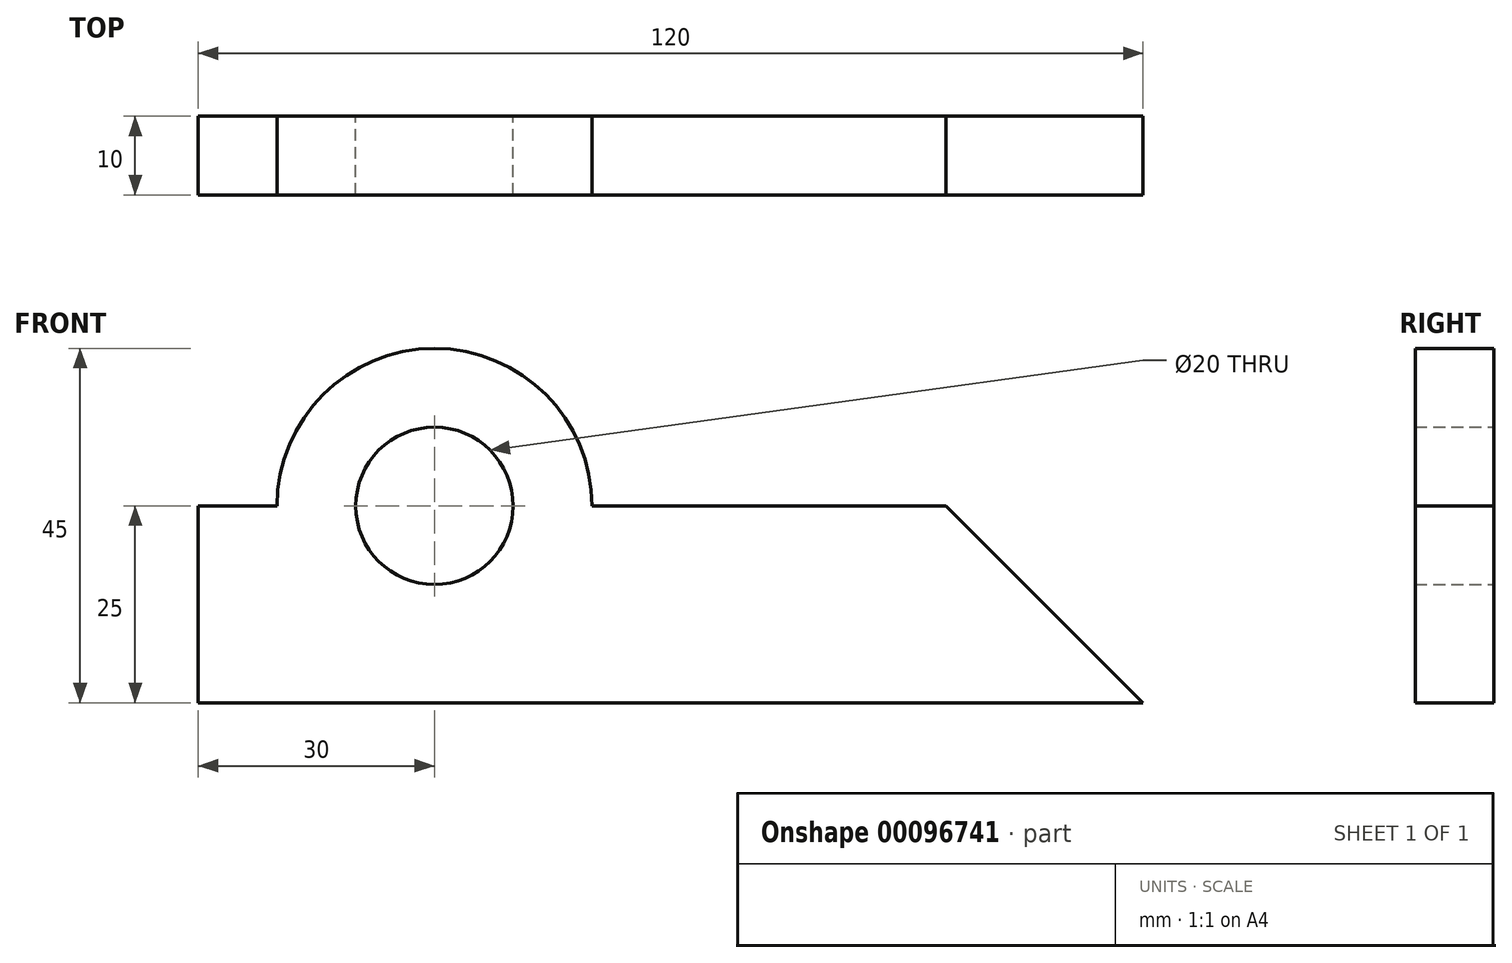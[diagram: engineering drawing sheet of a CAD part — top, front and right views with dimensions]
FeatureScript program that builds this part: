
annotation { "Feature Type Name" : "Feature", "Feature Type Description" : "" }
export const myFeature = defineFeature(function(context is Context, id is Id, definition is map)
    precondition{}
    {
        {
            var Q0;
            Q0=qCreatedBy(makeId("Front.planeOp"),FACE);
            var sketch = newSketch(context, id + "F0", { "sketchPlane" : qUnion([Q0])});
            skLineSegment(sketch, "E0", {"start": v(0, 0) * mm, "end": v(0, 25) * mm});
            skLineSegment(sketch, "E1", {"start": v(0, 0) * mm, "end": v(120, 0) * mm});
            skLineSegment(sketch, "E2", {"start": v(120, 0) * mm, "end": v(95, 25) * mm});
            skLineSegment(sketch, "E3", {"start": v(95, 25) * mm, "end": v(50, 25) * mm});
            skLineSegment(sketch, "E4", {"start": v(0, 25) * mm, "end": v(10, 25) * mm});
            skArc(sketch, "E5", {"start": v(50, 25) * mm, "mid": v(30, 45) * mm, "end": v(10, 25) * mm});
            skCircle(sketch, "E6", {"center": v(30, 25) * mm, "radius": 10 * mm});
            skSolve(sketch);
        }
        {
            var Q0;
            Q0 = qSketchRegion(id + "F0", true);
            extrude(context, id + "F1", {"entities" : qUnion([Q0]), "depth" : 10 * mm});
        }
    });
